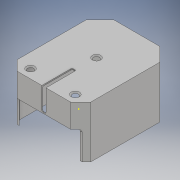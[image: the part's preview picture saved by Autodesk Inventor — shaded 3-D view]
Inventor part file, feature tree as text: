
AUTODESK INVENTOR PART (.ipt)
format: ipt  version: 2017 (Build 210142000, 142)  size: 292,864 bytes
history: native  units: mm
features: sketch x12, extrude x11, other x6, fillet x4, hole x3, projected_geometry x1
ambient origin geometry x8: Origin, YZ Plane, XZ Plane, XY Plane, X Axis, Y Axis, Z Axis, Center Point
bodies: Body1 (feature_tree)
feature tree (37):
  other  "Твердое тело1"
  sketch  "Эскиз1"
  extrude  "Выдавливание1"  Depth=60.0mm
  extrude  "Выдавливание2"  Depth=77.0mm
  fillet  "Сопряжение1"  Radius=11.0mm
  extrude  "Выдавливание3"  Depth=11.0mm
  extrude  "Выдавливание4"  Depth=8.5mm
  extrude  "Выдавливание5"  Depth=8.5mm
  other  "Комбинировать1"
  hole  "Отверстие4"  [1 undecoded]
  hole  "Отверстие5"  [1 undecoded]
  hole  "Отверстие6"  [1 undecoded]
  fillet  "Сопряжение2"  Radius=11.0mm
  fillet  "Сопряжение3"  Radius=1.2mm
  extrude  "Выдавливание6"  Depth=1.0mm TaperAngle=0.0deg
  extrude  "Выдавливание7"  Depth=43.0mm TaperAngle=0.0deg
  extrude  "Выдавливание8"  Depth=1.0mm
  other  "Комбинировать2"
  fillet  "Сопряжение4"  Radius=3.5mm
  extrude  "Выдавливание9"  Depth=25.0mm
  sketch  "Эскиз8"
  sketch  "Эскиз9"
  sketch  "Эскиз10"
  extrude  "Выдавливание10"  Depth=18.0mm TaperAngle=0.0deg
  other  "РабПлоскость1"
  extrude  "Выдавливание11"  Depth=17.0mm TaperAngle=0.0deg
  other  "Твердое тело2"
  sketch  "Эскиз2"
  sketch  "Эскиз3"
  sketch  "Эскиз4"
  other  "Твердое тело3"
  sketch  "Эскиз5"
  sketch  "Эскиз6"
  sketch  "Эскиз7"
  sketch  "Эскиз11"
  projected_geometry  "Спроецированная петля1"
  sketch  "Эскиз12"
note: 3 required parameter values undecoded (feature->parameter linkage not recoverable at this tier; creation-order binding heuristic only, values carry confidence <= 0.55)
